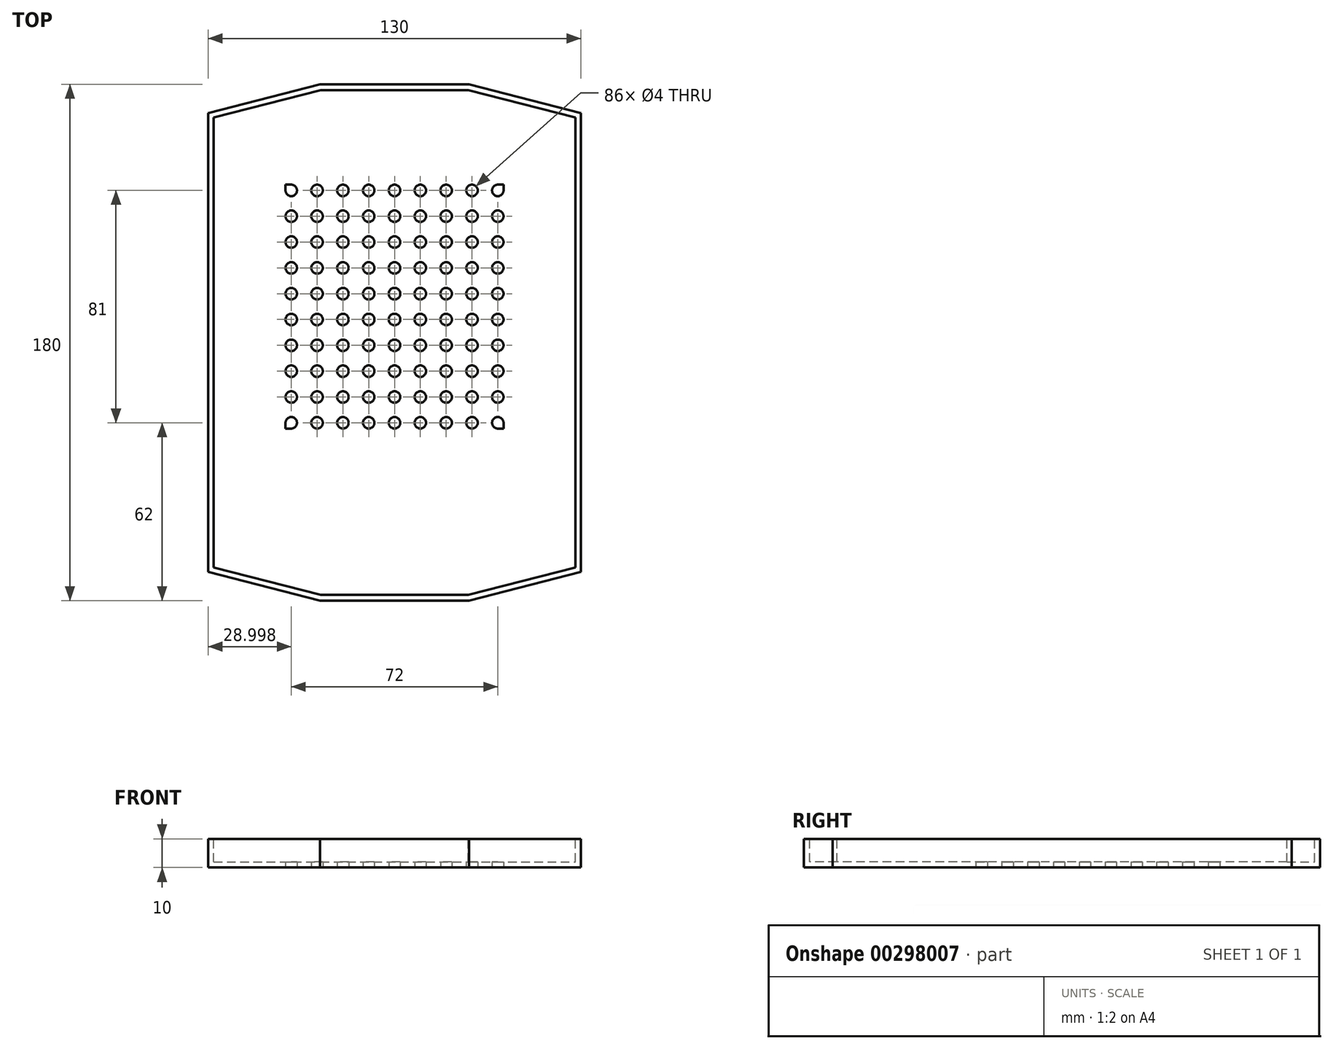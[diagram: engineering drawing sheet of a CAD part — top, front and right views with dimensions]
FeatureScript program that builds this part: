
annotation { "Feature Type Name" : "Feature", "Feature Type Description" : "" }
export const myFeature = defineFeature(function(context is Context, id is Id, definition is map)
    precondition{}
    {
        {
            var Q0;
            Q0=qCreatedBy(makeId("Top.planeOp"),FACE);
            var sketch = newSketch(context, id + "F0", { "sketchPlane" : qUnion([Q0])});
            skLineSegment(sketch, "E0.bottom", {"start": v(-77.32, -10) * mm, "end": v(52.68, -10) * mm});
            skLineSegment(sketch, "E0.top", {"start": v(-77.32, 170) * mm, "end": v(52.68, 170) * mm});
            skLineSegment(sketch, "E0.left", {"start": v(-77.32, -10) * mm, "end": v(-77.32, 170) * mm});
            skLineSegment(sketch, "E0.right", {"start": v(52.68, -10) * mm, "end": v(52.68, 170) * mm});
            skPoint(sketch, "E1", {"position": v(-38.32, 170) * mm});
            skPoint(sketch, "E2", {"position": v(-77.32, 160) * mm});
            skPoint(sketch, "E3", {"position": v(52.68, 160) * mm});
            skPoint(sketch, "E4", {"position": v(13.68, 170) * mm});
            skLineSegment(sketch, "E5", {"start": v(-77.32, 160) * mm, "end": v(-38.32, 170) * mm});
            skLineSegment(sketch, "E6", {"start": v(13.68, 170) * mm, "end": v(52.68, 160) * mm});
            skPoint(sketch, "E7", {"position": v(-77.32, 0) * mm});
            skPoint(sketch, "E8", {"position": v(-38.32, -10) * mm});
            skPoint(sketch, "E9", {"position": v(13.68, -10) * mm});
            skPoint(sketch, "E10", {"position": v(52.68, 0) * mm});
            skLineSegment(sketch, "E11", {"start": v(-77.32, 0) * mm, "end": v(-38.32, -10) * mm});
            skLineSegment(sketch, "E12", {"start": v(13.68, -10) * mm, "end": v(52.68, 0) * mm});
            skLineSegment(sketch, "E13.bottom", {"start": v(-50.32, 135) * mm, "end": v(25.68, 135) * mm});
            skLineSegment(sketch, "E13.top", {"start": v(-50.32, 50) * mm, "end": v(25.68, 50) * mm});
            skLineSegment(sketch, "E13.left", {"start": v(-50.32, 135) * mm, "end": v(-50.32, 50) * mm});
            skLineSegment(sketch, "E13.right", {"start": v(25.68, 135) * mm, "end": v(25.68, 50) * mm});
            skCircle(sketch, "E14", {"center": v(-48.32, 133) * mm, "radius": 2 * mm});
            skCircle(sketch, "E15", {"center": v(-39.32, 133) * mm, "radius": 2 * mm});
            skCircle(sketch, "E16", {"center": v(-30.32, 133) * mm, "radius": 2 * mm});
            skCircle(sketch, "E17", {"center": v(-21.32, 133) * mm, "radius": 2 * mm});
            skCircle(sketch, "E18", {"center": v(-12.32, 133) * mm, "radius": 2 * mm});
            skCircle(sketch, "E19", {"center": v(-3.32, 133) * mm, "radius": 2 * mm});
            skCircle(sketch, "E20", {"center": v(5.68, 133) * mm, "radius": 2 * mm});
            skCircle(sketch, "E21", {"center": v(14.68, 133) * mm, "radius": 2 * mm});
            skCircle(sketch, "E22", {"center": v(23.68, 133) * mm, "radius": 2 * mm});
            skCircle(sketch, "E23", {"center": v(-48.32, 124) * mm, "radius": 2 * mm});
            skCircle(sketch, "E24", {"center": v(-39.32, 124) * mm, "radius": 2 * mm});
            skCircle(sketch, "E25", {"center": v(-30.32, 124) * mm, "radius": 2 * mm});
            skCircle(sketch, "E26", {"center": v(-21.32, 124) * mm, "radius": 2 * mm});
            skCircle(sketch, "E27", {"center": v(-12.32, 124) * mm, "radius": 2 * mm});
            skCircle(sketch, "E28", {"center": v(-3.32, 124) * mm, "radius": 2 * mm});
            skCircle(sketch, "E29", {"center": v(5.68, 124) * mm, "radius": 2 * mm});
            skCircle(sketch, "E30", {"center": v(14.68, 124) * mm, "radius": 2 * mm});
            skCircle(sketch, "E31", {"center": v(23.68, 124) * mm, "radius": 2 * mm});
            skCircle(sketch, "E32", {"center": v(-48.32, 115) * mm, "radius": 2 * mm});
            skCircle(sketch, "E33", {"center": v(-39.32, 115) * mm, "radius": 2 * mm});
            skCircle(sketch, "E34", {"center": v(-30.32, 115) * mm, "radius": 2 * mm});
            skCircle(sketch, "E35", {"center": v(-21.32, 115) * mm, "radius": 2 * mm});
            skCircle(sketch, "E36", {"center": v(-12.32, 115) * mm, "radius": 2 * mm});
            skCircle(sketch, "E37", {"center": v(-3.32, 115) * mm, "radius": 2 * mm});
            skCircle(sketch, "E38", {"center": v(5.68, 115) * mm, "radius": 2 * mm});
            skCircle(sketch, "E39", {"center": v(14.68, 115) * mm, "radius": 2 * mm});
            skCircle(sketch, "E40", {"center": v(23.68, 115) * mm, "radius": 2 * mm});
            skCircle(sketch, "E41", {"center": v(-48.32, 106) * mm, "radius": 2 * mm});
            skCircle(sketch, "E42", {"center": v(-39.32, 106) * mm, "radius": 2 * mm});
            skCircle(sketch, "E43", {"center": v(-30.32, 106) * mm, "radius": 2 * mm});
            skCircle(sketch, "E44", {"center": v(-21.32, 106) * mm, "radius": 2 * mm});
            skCircle(sketch, "E45", {"center": v(-12.32, 106) * mm, "radius": 2 * mm});
            skCircle(sketch, "E46", {"center": v(-3.32, 106) * mm, "radius": 2 * mm});
            skCircle(sketch, "E47", {"center": v(5.68, 106) * mm, "radius": 2 * mm});
            skCircle(sketch, "E48", {"center": v(14.68, 106) * mm, "radius": 2 * mm});
            skCircle(sketch, "E49", {"center": v(23.68, 106) * mm, "radius": 2 * mm});
            skCircle(sketch, "E50", {"center": v(-48.32, 97) * mm, "radius": 2 * mm});
            skCircle(sketch, "E51", {"center": v(-39.32, 97) * mm, "radius": 2 * mm});
            skCircle(sketch, "E52", {"center": v(-30.32, 97) * mm, "radius": 2 * mm});
            skCircle(sketch, "E53", {"center": v(-21.32, 97) * mm, "radius": 2 * mm});
            skCircle(sketch, "E54", {"center": v(-12.32, 97) * mm, "radius": 2 * mm});
            skCircle(sketch, "E55", {"center": v(-3.32, 97) * mm, "radius": 2 * mm});
            skCircle(sketch, "E56", {"center": v(5.68, 97) * mm, "radius": 2 * mm});
            skCircle(sketch, "E57", {"center": v(14.68, 97) * mm, "radius": 2 * mm});
            skCircle(sketch, "E58", {"center": v(23.68, 97) * mm, "radius": 2 * mm});
            skCircle(sketch, "E59", {"center": v(-48.32, 88) * mm, "radius": 2 * mm});
            skCircle(sketch, "E60", {"center": v(-39.32, 88) * mm, "radius": 2 * mm});
            skCircle(sketch, "E61", {"center": v(-30.32, 88) * mm, "radius": 2 * mm});
            skCircle(sketch, "E62", {"center": v(-21.32, 88) * mm, "radius": 2 * mm});
            skCircle(sketch, "E63", {"center": v(-12.32, 88) * mm, "radius": 2 * mm});
            skCircle(sketch, "E64", {"center": v(-3.32, 88) * mm, "radius": 2 * mm});
            skCircle(sketch, "E65", {"center": v(5.68, 88) * mm, "radius": 2 * mm});
            skCircle(sketch, "E66", {"center": v(14.68, 88) * mm, "radius": 2 * mm});
            skCircle(sketch, "E67", {"center": v(23.68, 88) * mm, "radius": 2 * mm});
            skCircle(sketch, "E68", {"center": v(-48.32, 79) * mm, "radius": 2 * mm});
            skCircle(sketch, "E69", {"center": v(-39.32, 79) * mm, "radius": 2 * mm});
            skCircle(sketch, "E70", {"center": v(-30.32, 79) * mm, "radius": 2 * mm});
            skCircle(sketch, "E71", {"center": v(-21.32, 79) * mm, "radius": 2 * mm});
            skCircle(sketch, "E72", {"center": v(-12.32, 79) * mm, "radius": 2 * mm});
            skCircle(sketch, "E73", {"center": v(-3.32, 79) * mm, "radius": 2 * mm});
            skCircle(sketch, "E74", {"center": v(5.68, 79) * mm, "radius": 2 * mm});
            skCircle(sketch, "E75", {"center": v(14.68, 79) * mm, "radius": 2 * mm});
            skCircle(sketch, "E76", {"center": v(23.68, 79) * mm, "radius": 2 * mm});
            skCircle(sketch, "E77", {"center": v(-48.32, 70) * mm, "radius": 2 * mm});
            skCircle(sketch, "E78", {"center": v(-39.32, 70) * mm, "radius": 2 * mm});
            skCircle(sketch, "E79", {"center": v(-30.32, 70) * mm, "radius": 2 * mm});
            skCircle(sketch, "E80", {"center": v(-21.32, 70) * mm, "radius": 2 * mm});
            skCircle(sketch, "E81", {"center": v(-12.32, 70) * mm, "radius": 2 * mm});
            skCircle(sketch, "E82", {"center": v(-3.32, 70) * mm, "radius": 2 * mm});
            skCircle(sketch, "E83", {"center": v(5.68, 70) * mm, "radius": 2 * mm});
            skCircle(sketch, "E84", {"center": v(14.68, 70) * mm, "radius": 2 * mm});
            skCircle(sketch, "E85", {"center": v(23.68, 70) * mm, "radius": 2 * mm});
            skCircle(sketch, "E86", {"center": v(-48.32, 61) * mm, "radius": 2 * mm});
            skCircle(sketch, "E87", {"center": v(-39.32, 61) * mm, "radius": 2 * mm});
            skCircle(sketch, "E88", {"center": v(-30.32, 61) * mm, "radius": 2 * mm});
            skCircle(sketch, "E89", {"center": v(-21.32, 61) * mm, "radius": 2 * mm});
            skCircle(sketch, "E90", {"center": v(-12.32, 61) * mm, "radius": 2 * mm});
            skCircle(sketch, "E91", {"center": v(-3.32, 61) * mm, "radius": 2 * mm});
            skCircle(sketch, "E92", {"center": v(5.68, 61) * mm, "radius": 2 * mm});
            skCircle(sketch, "E93", {"center": v(14.68, 61) * mm, "radius": 2 * mm});
            skCircle(sketch, "E94", {"center": v(23.68, 61) * mm, "radius": 2 * mm});
            skCircle(sketch, "E95", {"center": v(-48.32, 52) * mm, "radius": 2 * mm});
            skCircle(sketch, "E96", {"center": v(-39.32, 52) * mm, "radius": 2 * mm});
            skCircle(sketch, "E97", {"center": v(-30.32, 52) * mm, "radius": 2 * mm});
            skCircle(sketch, "E98", {"center": v(-21.32, 52) * mm, "radius": 2 * mm});
            skCircle(sketch, "E99", {"center": v(-12.32, 52) * mm, "radius": 2 * mm});
            skCircle(sketch, "E100", {"center": v(-3.32, 52) * mm, "radius": 2 * mm});
            skCircle(sketch, "E101", {"center": v(5.68, 52) * mm, "radius": 2 * mm});
            skCircle(sketch, "E102", {"center": v(14.68, 52) * mm, "radius": 2 * mm});
            skCircle(sketch, "E103", {"center": v(23.68, 52) * mm, "radius": 2 * mm});
            skSolve(sketch);
        }
        {
            var Q0;
            {var subQ39=sQuery(id+"F0.wireOp",EDGE,"E5");Q0=makeQuery(id+"F0.imprint","IMPRINT",FACE,{"disambiguationData":[TD([[makeQuery(id+"F0.imprint","IMPRINT",EDGE,{"derivedFrom":subQ39}),-1.0]])]});}
            var Q1;
            {var subQ43=sQuery(id+"F0.wireOp",EDGE,"E15");Q1=makeQuery(id+"F0.imprint","IMPRINT",FACE,{"disambiguationData":[TD([[makeQuery(id+"F0.imprint","IMPRINT",EDGE,{"derivedFrom":subQ43}),-1.0]])]});}
            extrude(context, id + "F1", {"entities" : qUnion([Q0, Q1]), "depth" : 10 * mm});
        }
        {
            var Q0;
            Q0=makeQuery(id+"F1.opExtrude","CAP_FACE",FACE,{"disambiguationData":[OSD([sQuery(id+"F0.wireOp",EDGE,"E0.bottom"),sQuery(id+"F0.wireOp",EDGE,"E0.top"),sQuery(id+"F0.wireOp",EDGE,"E0.left"),sQuery(id+"F0.wireOp",EDGE,"E0.right"),sQuery(id+"F0.wireOp",EDGE,"E5"),sQuery(id+"F0.wireOp",EDGE,"E6"),sQuery(id+"F0.wireOp",EDGE,"E11"),sQuery(id+"F0.wireOp",EDGE,"E12"),sQuery(id+"F0.wireOp",EDGE,"E13.bottom"),sQuery(id+"F0.wireOp",EDGE,"E13.top"),sQuery(id+"F0.wireOp",EDGE,"E13.left"),sQuery(id+"F0.wireOp",EDGE,"E13.right"),sQuery(id+"F0.wireOp",EDGE,"E14"),sQuery(id+"F0.wireOp",EDGE,"E15"),sQuery(id+"F0.wireOp",EDGE,"E16"),sQuery(id+"F0.wireOp",EDGE,"E17"),sQuery(id+"F0.wireOp",EDGE,"E18"),sQuery(id+"F0.wireOp",EDGE,"E19"),sQuery(id+"F0.wireOp",EDGE,"E20"),sQuery(id+"F0.wireOp",EDGE,"E21"),sQuery(id+"F0.wireOp",EDGE,"E22"),sQuery(id+"F0.wireOp",EDGE,"E23"),sQuery(id+"F0.wireOp",EDGE,"E24"),sQuery(id+"F0.wireOp",EDGE,"E25"),sQuery(id+"F0.wireOp",EDGE,"E26"),sQuery(id+"F0.wireOp",EDGE,"E27"),sQuery(id+"F0.wireOp",EDGE,"E28"),sQuery(id+"F0.wireOp",EDGE,"E29"),sQuery(id+"F0.wireOp",EDGE,"E30"),sQuery(id+"F0.wireOp",EDGE,"E31"),sQuery(id+"F0.wireOp",EDGE,"E32"),sQuery(id+"F0.wireOp",EDGE,"E33"),sQuery(id+"F0.wireOp",EDGE,"E34"),sQuery(id+"F0.wireOp",EDGE,"E35"),sQuery(id+"F0.wireOp",EDGE,"E36"),sQuery(id+"F0.wireOp",EDGE,"E37"),sQuery(id+"F0.wireOp",EDGE,"E38"),sQuery(id+"F0.wireOp",EDGE,"E39"),sQuery(id+"F0.wireOp",EDGE,"E40"),sQuery(id+"F0.wireOp",EDGE,"E41"),sQuery(id+"F0.wireOp",EDGE,"E42"),sQuery(id+"F0.wireOp",EDGE,"E43"),sQuery(id+"F0.wireOp",EDGE,"E44"),sQuery(id+"F0.wireOp",EDGE,"E45"),sQuery(id+"F0.wireOp",EDGE,"E46"),sQuery(id+"F0.wireOp",EDGE,"E47"),sQuery(id+"F0.wireOp",EDGE,"E48"),sQuery(id+"F0.wireOp",EDGE,"E49"),sQuery(id+"F0.wireOp",EDGE,"E50"),sQuery(id+"F0.wireOp",EDGE,"E51"),sQuery(id+"F0.wireOp",EDGE,"E52"),sQuery(id+"F0.wireOp",EDGE,"E53"),sQuery(id+"F0.wireOp",EDGE,"E54"),sQuery(id+"F0.wireOp",EDGE,"E55"),sQuery(id+"F0.wireOp",EDGE,"E56"),sQuery(id+"F0.wireOp",EDGE,"E57"),sQuery(id+"F0.wireOp",EDGE,"E58"),sQuery(id+"F0.wireOp",EDGE,"E59"),sQuery(id+"F0.wireOp",EDGE,"E60"),sQuery(id+"F0.wireOp",EDGE,"E61"),sQuery(id+"F0.wireOp",EDGE,"E62"),sQuery(id+"F0.wireOp",EDGE,"E63"),sQuery(id+"F0.wireOp",EDGE,"E64"),sQuery(id+"F0.wireOp",EDGE,"E65"),sQuery(id+"F0.wireOp",EDGE,"E66"),sQuery(id+"F0.wireOp",EDGE,"E67"),sQuery(id+"F0.wireOp",EDGE,"E68"),sQuery(id+"F0.wireOp",EDGE,"E69"),sQuery(id+"F0.wireOp",EDGE,"E70"),sQuery(id+"F0.wireOp",EDGE,"E71"),sQuery(id+"F0.wireOp",EDGE,"E72"),sQuery(id+"F0.wireOp",EDGE,"E73"),sQuery(id+"F0.wireOp",EDGE,"E74"),sQuery(id+"F0.wireOp",EDGE,"E75"),sQuery(id+"F0.wireOp",EDGE,"E76"),sQuery(id+"F0.wireOp",EDGE,"E77"),sQuery(id+"F0.wireOp",EDGE,"E78"),sQuery(id+"F0.wireOp",EDGE,"E79"),sQuery(id+"F0.wireOp",EDGE,"E80"),sQuery(id+"F0.wireOp",EDGE,"E81"),sQuery(id+"F0.wireOp",EDGE,"E82"),sQuery(id+"F0.wireOp",EDGE,"E83"),sQuery(id+"F0.wireOp",EDGE,"E84"),sQuery(id+"F0.wireOp",EDGE,"E85"),sQuery(id+"F0.wireOp",EDGE,"E86"),sQuery(id+"F0.wireOp",EDGE,"E87"),sQuery(id+"F0.wireOp",EDGE,"E88"),sQuery(id+"F0.wireOp",EDGE,"E89"),sQuery(id+"F0.wireOp",EDGE,"E90"),sQuery(id+"F0.wireOp",EDGE,"E91"),sQuery(id+"F0.wireOp",EDGE,"E92"),sQuery(id+"F0.wireOp",EDGE,"E93"),sQuery(id+"F0.wireOp",EDGE,"E94"),sQuery(id+"F0.wireOp",EDGE,"E95"),sQuery(id+"F0.wireOp",EDGE,"E96"),sQuery(id+"F0.wireOp",EDGE,"E97"),sQuery(id+"F0.wireOp",EDGE,"E98"),sQuery(id+"F0.wireOp",EDGE,"E99"),sQuery(id+"F0.wireOp",EDGE,"E100"),sQuery(id+"F0.wireOp",EDGE,"E101"),sQuery(id+"F0.wireOp",EDGE,"E102"),sQuery(id+"F0.wireOp",EDGE,"E103")])],"isStart":false});
            var sketch = newSketch(context, id + "F2", { "sketchPlane" : qUnion([Q0])});
            skLineSegment(sketch, "E104.bottom", {"start": v(-75.32, 168) * mm, "end": v(50.68, 168) * mm});
            skLineSegment(sketch, "E104.top", {"start": v(-75.32, -8) * mm, "end": v(50.68, -8) * mm});
            skLineSegment(sketch, "E104.left", {"start": v(-75.32, 168) * mm, "end": v(-75.32, -8) * mm});
            skLineSegment(sketch, "E104.right", {"start": v(50.68, 168) * mm, "end": v(50.68, -8) * mm});
            skLineSegment(sketch, "E105", {"start": v(-75.32, 158.45) * mm, "end": v(-38.07, 168) * mm});
            skLineSegment(sketch, "E106", {"start": v(13.43, 168) * mm, "end": v(50.68, 158.45) * mm});
            skLineSegment(sketch, "E107", {"start": v(-75.32, 1.55) * mm, "end": v(-38.07, -8) * mm});
            skLineSegment(sketch, "E108", {"start": v(13.43, -8) * mm, "end": v(50.68, 1.55) * mm});
            skSolve(sketch);
        }
        {
            var Q0;
            {var subQ3=sQuery(id+"F0.wireOp",EDGE,"E14");Q0=makeQuery(id+"F2.imprint","IMPRINT",FACE,{"disambiguationData":[TD([[makeQuery(id+"F2.imprint","IMPRINT",EDGE,{"derivedFrom":makeQuery(id+"F1.opExtrude","CAP_EDGE",EDGE,{"disambiguationData":[OSD([subQ3])],"isStart":false})}),1.0]])]});}
            var Q1;
            {var subQ3=sQuery(id+"F0.wireOp",EDGE,"E22");Q1=makeQuery(id+"F2.imprint","IMPRINT",FACE,{"disambiguationData":[TD([[makeQuery(id+"F2.imprint","IMPRINT",EDGE,{"derivedFrom":makeQuery(id+"F1.opExtrude","CAP_EDGE",EDGE,{"disambiguationData":[OSD([subQ3])],"isStart":false})}),1.0]])]});}
            var Q2;
            {var subQ3=sQuery(id+"F0.wireOp",EDGE,"E95");Q2=makeQuery(id+"F2.imprint","IMPRINT",FACE,{"disambiguationData":[TD([[makeQuery(id+"F2.imprint","IMPRINT",EDGE,{"derivedFrom":makeQuery(id+"F1.opExtrude","CAP_EDGE",EDGE,{"disambiguationData":[OSD([subQ3])],"isStart":false})}),1.0]])]});}
            var Q3;
            {var subQ3=sQuery(id+"F0.wireOp",EDGE,"E103");Q3=makeQuery(id+"F2.imprint","IMPRINT",FACE,{"disambiguationData":[TD([[makeQuery(id+"F2.imprint","IMPRINT",EDGE,{"derivedFrom":makeQuery(id+"F1.opExtrude","CAP_EDGE",EDGE,{"disambiguationData":[OSD([subQ3])],"isStart":false})}),1.0]])]});}
            var Q4;
            Q4=makeQuery(id+"F2.imprint","IMPRINT",FACE,{"disambiguationData":[TD([[makeQuery(id+"F2.imprint","IMPRINT",EDGE,{"derivedFrom":makeQuery(id+"F1.opExtrude","CAP_EDGE",EDGE,{"disambiguationData":[OSD([sQuery(id+"F0.wireOp",EDGE,"E15")])],"isStart":false})}),1.0]])]});
            var Q5;
            Q5=makeQuery(id+"F2.imprint","IMPRINT",FACE,{"disambiguationData":[TD([[makeQuery(id+"F2.imprint","IMPRINT",EDGE,{"derivedFrom":makeQuery(id+"F1.opExtrude","CAP_EDGE",EDGE,{"disambiguationData":[OSD([sQuery(id+"F0.wireOp",EDGE,"E16")])],"isStart":false})}),1.0]])]});
            var Q6;
            Q6=makeQuery(id+"F2.imprint","IMPRINT",FACE,{"disambiguationData":[TD([[makeQuery(id+"F2.imprint","IMPRINT",EDGE,{"derivedFrom":makeQuery(id+"F1.opExtrude","CAP_EDGE",EDGE,{"disambiguationData":[OSD([sQuery(id+"F0.wireOp",EDGE,"E17")])],"isStart":false})}),1.0]])]});
            var Q7;
            Q7=makeQuery(id+"F2.imprint","IMPRINT",FACE,{"disambiguationData":[TD([[makeQuery(id+"F2.imprint","IMPRINT",EDGE,{"derivedFrom":makeQuery(id+"F1.opExtrude","CAP_EDGE",EDGE,{"disambiguationData":[OSD([sQuery(id+"F0.wireOp",EDGE,"E18")])],"isStart":false})}),1.0]])]});
            var Q8;
            Q8=makeQuery(id+"F2.imprint","IMPRINT",FACE,{"disambiguationData":[TD([[makeQuery(id+"F2.imprint","IMPRINT",EDGE,{"derivedFrom":makeQuery(id+"F1.opExtrude","CAP_EDGE",EDGE,{"disambiguationData":[OSD([sQuery(id+"F0.wireOp",EDGE,"E19")])],"isStart":false})}),1.0]])]});
            var Q9;
            Q9=makeQuery(id+"F2.imprint","IMPRINT",FACE,{"disambiguationData":[TD([[makeQuery(id+"F2.imprint","IMPRINT",EDGE,{"derivedFrom":makeQuery(id+"F1.opExtrude","CAP_EDGE",EDGE,{"disambiguationData":[OSD([sQuery(id+"F0.wireOp",EDGE,"E20")])],"isStart":false})}),1.0]])]});
            var Q10;
            Q10=makeQuery(id+"F2.imprint","IMPRINT",FACE,{"disambiguationData":[TD([[makeQuery(id+"F2.imprint","IMPRINT",EDGE,{"derivedFrom":makeQuery(id+"F1.opExtrude","CAP_EDGE",EDGE,{"disambiguationData":[OSD([sQuery(id+"F0.wireOp",EDGE,"E21")])],"isStart":false})}),1.0]])]});
            var Q11;
            Q11=makeQuery(id+"F2.imprint","IMPRINT",FACE,{"disambiguationData":[TD([[makeQuery(id+"F2.imprint","IMPRINT",EDGE,{"derivedFrom":makeQuery(id+"F1.opExtrude","CAP_EDGE",EDGE,{"disambiguationData":[OSD([sQuery(id+"F0.wireOp",EDGE,"E23")])],"isStart":false})}),1.0]])]});
            var Q12;
            Q12=makeQuery(id+"F2.imprint","IMPRINT",FACE,{"disambiguationData":[TD([[makeQuery(id+"F2.imprint","IMPRINT",EDGE,{"derivedFrom":makeQuery(id+"F1.opExtrude","CAP_EDGE",EDGE,{"disambiguationData":[OSD([sQuery(id+"F0.wireOp",EDGE,"E24")])],"isStart":false})}),1.0]])]});
            var Q13;
            Q13=makeQuery(id+"F2.imprint","IMPRINT",FACE,{"disambiguationData":[TD([[makeQuery(id+"F2.imprint","IMPRINT",EDGE,{"derivedFrom":makeQuery(id+"F1.opExtrude","CAP_EDGE",EDGE,{"disambiguationData":[OSD([sQuery(id+"F0.wireOp",EDGE,"E25")])],"isStart":false})}),1.0]])]});
            var Q14;
            Q14=makeQuery(id+"F2.imprint","IMPRINT",FACE,{"disambiguationData":[TD([[makeQuery(id+"F2.imprint","IMPRINT",EDGE,{"derivedFrom":makeQuery(id+"F1.opExtrude","CAP_EDGE",EDGE,{"disambiguationData":[OSD([sQuery(id+"F0.wireOp",EDGE,"E26")])],"isStart":false})}),1.0]])]});
            var Q15;
            Q15=makeQuery(id+"F2.imprint","IMPRINT",FACE,{"disambiguationData":[TD([[makeQuery(id+"F2.imprint","IMPRINT",EDGE,{"derivedFrom":makeQuery(id+"F1.opExtrude","CAP_EDGE",EDGE,{"disambiguationData":[OSD([sQuery(id+"F0.wireOp",EDGE,"E27")])],"isStart":false})}),1.0]])]});
            var Q16;
            Q16=makeQuery(id+"F2.imprint","IMPRINT",FACE,{"disambiguationData":[TD([[makeQuery(id+"F2.imprint","IMPRINT",EDGE,{"derivedFrom":makeQuery(id+"F1.opExtrude","CAP_EDGE",EDGE,{"disambiguationData":[OSD([sQuery(id+"F0.wireOp",EDGE,"E28")])],"isStart":false})}),1.0]])]});
            var Q17;
            Q17=makeQuery(id+"F2.imprint","IMPRINT",FACE,{"disambiguationData":[TD([[makeQuery(id+"F2.imprint","IMPRINT",EDGE,{"derivedFrom":makeQuery(id+"F1.opExtrude","CAP_EDGE",EDGE,{"disambiguationData":[OSD([sQuery(id+"F0.wireOp",EDGE,"E29")])],"isStart":false})}),1.0]])]});
            var Q18;
            Q18=makeQuery(id+"F2.imprint","IMPRINT",FACE,{"disambiguationData":[TD([[makeQuery(id+"F2.imprint","IMPRINT",EDGE,{"derivedFrom":makeQuery(id+"F1.opExtrude","CAP_EDGE",EDGE,{"disambiguationData":[OSD([sQuery(id+"F0.wireOp",EDGE,"E30")])],"isStart":false})}),1.0]])]});
            var Q19;
            Q19=makeQuery(id+"F2.imprint","IMPRINT",FACE,{"disambiguationData":[TD([[makeQuery(id+"F2.imprint","IMPRINT",EDGE,{"derivedFrom":makeQuery(id+"F1.opExtrude","CAP_EDGE",EDGE,{"disambiguationData":[OSD([sQuery(id+"F0.wireOp",EDGE,"E31")])],"isStart":false})}),1.0]])]});
            var Q20;
            Q20=makeQuery(id+"F2.imprint","IMPRINT",FACE,{"disambiguationData":[TD([[makeQuery(id+"F2.imprint","IMPRINT",EDGE,{"derivedFrom":makeQuery(id+"F1.opExtrude","CAP_EDGE",EDGE,{"disambiguationData":[OSD([sQuery(id+"F0.wireOp",EDGE,"E32")])],"isStart":false})}),1.0]])]});
            var Q21;
            Q21=makeQuery(id+"F2.imprint","IMPRINT",FACE,{"disambiguationData":[TD([[makeQuery(id+"F2.imprint","IMPRINT",EDGE,{"derivedFrom":makeQuery(id+"F1.opExtrude","CAP_EDGE",EDGE,{"disambiguationData":[OSD([sQuery(id+"F0.wireOp",EDGE,"E33")])],"isStart":false})}),1.0]])]});
            var Q22;
            Q22=makeQuery(id+"F2.imprint","IMPRINT",FACE,{"disambiguationData":[TD([[makeQuery(id+"F2.imprint","IMPRINT",EDGE,{"derivedFrom":makeQuery(id+"F1.opExtrude","CAP_EDGE",EDGE,{"disambiguationData":[OSD([sQuery(id+"F0.wireOp",EDGE,"E34")])],"isStart":false})}),1.0]])]});
            var Q23;
            Q23=makeQuery(id+"F2.imprint","IMPRINT",FACE,{"disambiguationData":[TD([[makeQuery(id+"F2.imprint","IMPRINT",EDGE,{"derivedFrom":makeQuery(id+"F1.opExtrude","CAP_EDGE",EDGE,{"disambiguationData":[OSD([sQuery(id+"F0.wireOp",EDGE,"E35")])],"isStart":false})}),1.0]])]});
            var Q24;
            Q24=makeQuery(id+"F2.imprint","IMPRINT",FACE,{"disambiguationData":[TD([[makeQuery(id+"F2.imprint","IMPRINT",EDGE,{"derivedFrom":makeQuery(id+"F1.opExtrude","CAP_EDGE",EDGE,{"disambiguationData":[OSD([sQuery(id+"F0.wireOp",EDGE,"E36")])],"isStart":false})}),1.0]])]});
            var Q25;
            Q25=makeQuery(id+"F2.imprint","IMPRINT",FACE,{"disambiguationData":[TD([[makeQuery(id+"F2.imprint","IMPRINT",EDGE,{"derivedFrom":makeQuery(id+"F1.opExtrude","CAP_EDGE",EDGE,{"disambiguationData":[OSD([sQuery(id+"F0.wireOp",EDGE,"E37")])],"isStart":false})}),1.0]])]});
            var Q26;
            Q26=makeQuery(id+"F2.imprint","IMPRINT",FACE,{"disambiguationData":[TD([[makeQuery(id+"F2.imprint","IMPRINT",EDGE,{"derivedFrom":makeQuery(id+"F1.opExtrude","CAP_EDGE",EDGE,{"disambiguationData":[OSD([sQuery(id+"F0.wireOp",EDGE,"E38")])],"isStart":false})}),1.0]])]});
            var Q27;
            Q27=makeQuery(id+"F2.imprint","IMPRINT",FACE,{"disambiguationData":[TD([[makeQuery(id+"F2.imprint","IMPRINT",EDGE,{"derivedFrom":makeQuery(id+"F1.opExtrude","CAP_EDGE",EDGE,{"disambiguationData":[OSD([sQuery(id+"F0.wireOp",EDGE,"E39")])],"isStart":false})}),1.0]])]});
            var Q28;
            Q28=makeQuery(id+"F2.imprint","IMPRINT",FACE,{"disambiguationData":[TD([[makeQuery(id+"F2.imprint","IMPRINT",EDGE,{"derivedFrom":makeQuery(id+"F1.opExtrude","CAP_EDGE",EDGE,{"disambiguationData":[OSD([sQuery(id+"F0.wireOp",EDGE,"E40")])],"isStart":false})}),1.0]])]});
            var Q29;
            Q29=makeQuery(id+"F2.imprint","IMPRINT",FACE,{"disambiguationData":[TD([[makeQuery(id+"F2.imprint","IMPRINT",EDGE,{"derivedFrom":makeQuery(id+"F1.opExtrude","CAP_EDGE",EDGE,{"disambiguationData":[OSD([sQuery(id+"F0.wireOp",EDGE,"E41")])],"isStart":false})}),1.0]])]});
            var Q30;
            Q30=makeQuery(id+"F2.imprint","IMPRINT",FACE,{"disambiguationData":[TD([[makeQuery(id+"F2.imprint","IMPRINT",EDGE,{"derivedFrom":makeQuery(id+"F1.opExtrude","CAP_EDGE",EDGE,{"disambiguationData":[OSD([sQuery(id+"F0.wireOp",EDGE,"E42")])],"isStart":false})}),1.0]])]});
            var Q31;
            Q31=makeQuery(id+"F2.imprint","IMPRINT",FACE,{"disambiguationData":[TD([[makeQuery(id+"F2.imprint","IMPRINT",EDGE,{"derivedFrom":makeQuery(id+"F1.opExtrude","CAP_EDGE",EDGE,{"disambiguationData":[OSD([sQuery(id+"F0.wireOp",EDGE,"E43")])],"isStart":false})}),1.0]])]});
            var Q32;
            Q32=makeQuery(id+"F2.imprint","IMPRINT",FACE,{"disambiguationData":[TD([[makeQuery(id+"F2.imprint","IMPRINT",EDGE,{"derivedFrom":makeQuery(id+"F1.opExtrude","CAP_EDGE",EDGE,{"disambiguationData":[OSD([sQuery(id+"F0.wireOp",EDGE,"E44")])],"isStart":false})}),1.0]])]});
            var Q33;
            Q33=makeQuery(id+"F2.imprint","IMPRINT",FACE,{"disambiguationData":[TD([[makeQuery(id+"F2.imprint","IMPRINT",EDGE,{"derivedFrom":makeQuery(id+"F1.opExtrude","CAP_EDGE",EDGE,{"disambiguationData":[OSD([sQuery(id+"F0.wireOp",EDGE,"E45")])],"isStart":false})}),1.0]])]});
            var Q34;
            Q34=makeQuery(id+"F2.imprint","IMPRINT",FACE,{"disambiguationData":[TD([[makeQuery(id+"F2.imprint","IMPRINT",EDGE,{"derivedFrom":makeQuery(id+"F1.opExtrude","CAP_EDGE",EDGE,{"disambiguationData":[OSD([sQuery(id+"F0.wireOp",EDGE,"E46")])],"isStart":false})}),1.0]])]});
            var Q35;
            Q35=makeQuery(id+"F2.imprint","IMPRINT",FACE,{"disambiguationData":[TD([[makeQuery(id+"F2.imprint","IMPRINT",EDGE,{"derivedFrom":makeQuery(id+"F1.opExtrude","CAP_EDGE",EDGE,{"disambiguationData":[OSD([sQuery(id+"F0.wireOp",EDGE,"E47")])],"isStart":false})}),1.0]])]});
            var Q36;
            Q36=makeQuery(id+"F2.imprint","IMPRINT",FACE,{"disambiguationData":[TD([[makeQuery(id+"F2.imprint","IMPRINT",EDGE,{"derivedFrom":makeQuery(id+"F1.opExtrude","CAP_EDGE",EDGE,{"disambiguationData":[OSD([sQuery(id+"F0.wireOp",EDGE,"E48")])],"isStart":false})}),1.0]])]});
            var Q37;
            Q37=makeQuery(id+"F2.imprint","IMPRINT",FACE,{"disambiguationData":[TD([[makeQuery(id+"F2.imprint","IMPRINT",EDGE,{"derivedFrom":makeQuery(id+"F1.opExtrude","CAP_EDGE",EDGE,{"disambiguationData":[OSD([sQuery(id+"F0.wireOp",EDGE,"E49")])],"isStart":false})}),1.0]])]});
            var Q38;
            Q38=makeQuery(id+"F2.imprint","IMPRINT",FACE,{"disambiguationData":[TD([[makeQuery(id+"F2.imprint","IMPRINT",EDGE,{"derivedFrom":makeQuery(id+"F1.opExtrude","CAP_EDGE",EDGE,{"disambiguationData":[OSD([sQuery(id+"F0.wireOp",EDGE,"E50")])],"isStart":false})}),1.0]])]});
            var Q39;
            Q39=makeQuery(id+"F2.imprint","IMPRINT",FACE,{"disambiguationData":[TD([[makeQuery(id+"F2.imprint","IMPRINT",EDGE,{"derivedFrom":makeQuery(id+"F1.opExtrude","CAP_EDGE",EDGE,{"disambiguationData":[OSD([sQuery(id+"F0.wireOp",EDGE,"E51")])],"isStart":false})}),1.0]])]});
            var Q40;
            Q40=makeQuery(id+"F2.imprint","IMPRINT",FACE,{"disambiguationData":[TD([[makeQuery(id+"F2.imprint","IMPRINT",EDGE,{"derivedFrom":makeQuery(id+"F1.opExtrude","CAP_EDGE",EDGE,{"disambiguationData":[OSD([sQuery(id+"F0.wireOp",EDGE,"E52")])],"isStart":false})}),1.0]])]});
            var Q41;
            Q41=makeQuery(id+"F2.imprint","IMPRINT",FACE,{"disambiguationData":[TD([[makeQuery(id+"F2.imprint","IMPRINT",EDGE,{"derivedFrom":makeQuery(id+"F1.opExtrude","CAP_EDGE",EDGE,{"disambiguationData":[OSD([sQuery(id+"F0.wireOp",EDGE,"E53")])],"isStart":false})}),1.0]])]});
            var Q42;
            Q42=makeQuery(id+"F2.imprint","IMPRINT",FACE,{"disambiguationData":[TD([[makeQuery(id+"F2.imprint","IMPRINT",EDGE,{"derivedFrom":makeQuery(id+"F1.opExtrude","CAP_EDGE",EDGE,{"disambiguationData":[OSD([sQuery(id+"F0.wireOp",EDGE,"E54")])],"isStart":false})}),1.0]])]});
            var Q43;
            Q43=makeQuery(id+"F2.imprint","IMPRINT",FACE,{"disambiguationData":[TD([[makeQuery(id+"F2.imprint","IMPRINT",EDGE,{"derivedFrom":makeQuery(id+"F1.opExtrude","CAP_EDGE",EDGE,{"disambiguationData":[OSD([sQuery(id+"F0.wireOp",EDGE,"E55")])],"isStart":false})}),1.0]])]});
            var Q44;
            Q44=makeQuery(id+"F2.imprint","IMPRINT",FACE,{"disambiguationData":[TD([[makeQuery(id+"F2.imprint","IMPRINT",EDGE,{"derivedFrom":makeQuery(id+"F1.opExtrude","CAP_EDGE",EDGE,{"disambiguationData":[OSD([sQuery(id+"F0.wireOp",EDGE,"E56")])],"isStart":false})}),1.0]])]});
            var Q45;
            Q45=makeQuery(id+"F2.imprint","IMPRINT",FACE,{"disambiguationData":[TD([[makeQuery(id+"F2.imprint","IMPRINT",EDGE,{"derivedFrom":makeQuery(id+"F1.opExtrude","CAP_EDGE",EDGE,{"disambiguationData":[OSD([sQuery(id+"F0.wireOp",EDGE,"E57")])],"isStart":false})}),1.0]])]});
            var Q46;
            Q46=makeQuery(id+"F2.imprint","IMPRINT",FACE,{"disambiguationData":[TD([[makeQuery(id+"F2.imprint","IMPRINT",EDGE,{"derivedFrom":makeQuery(id+"F1.opExtrude","CAP_EDGE",EDGE,{"disambiguationData":[OSD([sQuery(id+"F0.wireOp",EDGE,"E58")])],"isStart":false})}),1.0]])]});
            var Q47;
            Q47=makeQuery(id+"F2.imprint","IMPRINT",FACE,{"disambiguationData":[TD([[makeQuery(id+"F2.imprint","IMPRINT",EDGE,{"derivedFrom":makeQuery(id+"F1.opExtrude","CAP_EDGE",EDGE,{"disambiguationData":[OSD([sQuery(id+"F0.wireOp",EDGE,"E59")])],"isStart":false})}),1.0]])]});
            var Q48;
            Q48=makeQuery(id+"F2.imprint","IMPRINT",FACE,{"disambiguationData":[TD([[makeQuery(id+"F2.imprint","IMPRINT",EDGE,{"derivedFrom":makeQuery(id+"F1.opExtrude","CAP_EDGE",EDGE,{"disambiguationData":[OSD([sQuery(id+"F0.wireOp",EDGE,"E60")])],"isStart":false})}),1.0]])]});
            var Q49;
            Q49=makeQuery(id+"F2.imprint","IMPRINT",FACE,{"disambiguationData":[TD([[makeQuery(id+"F2.imprint","IMPRINT",EDGE,{"derivedFrom":makeQuery(id+"F1.opExtrude","CAP_EDGE",EDGE,{"disambiguationData":[OSD([sQuery(id+"F0.wireOp",EDGE,"E61")])],"isStart":false})}),1.0]])]});
            var Q50;
            Q50=makeQuery(id+"F2.imprint","IMPRINT",FACE,{"disambiguationData":[TD([[makeQuery(id+"F2.imprint","IMPRINT",EDGE,{"derivedFrom":makeQuery(id+"F1.opExtrude","CAP_EDGE",EDGE,{"disambiguationData":[OSD([sQuery(id+"F0.wireOp",EDGE,"E62")])],"isStart":false})}),1.0]])]});
            var Q51;
            Q51=makeQuery(id+"F2.imprint","IMPRINT",FACE,{"disambiguationData":[TD([[makeQuery(id+"F2.imprint","IMPRINT",EDGE,{"derivedFrom":makeQuery(id+"F1.opExtrude","CAP_EDGE",EDGE,{"disambiguationData":[OSD([sQuery(id+"F0.wireOp",EDGE,"E63")])],"isStart":false})}),1.0]])]});
            var Q52;
            Q52=makeQuery(id+"F2.imprint","IMPRINT",FACE,{"disambiguationData":[TD([[makeQuery(id+"F2.imprint","IMPRINT",EDGE,{"derivedFrom":makeQuery(id+"F1.opExtrude","CAP_EDGE",EDGE,{"disambiguationData":[OSD([sQuery(id+"F0.wireOp",EDGE,"E64")])],"isStart":false})}),1.0]])]});
            var Q53;
            Q53=makeQuery(id+"F2.imprint","IMPRINT",FACE,{"disambiguationData":[TD([[makeQuery(id+"F2.imprint","IMPRINT",EDGE,{"derivedFrom":makeQuery(id+"F1.opExtrude","CAP_EDGE",EDGE,{"disambiguationData":[OSD([sQuery(id+"F0.wireOp",EDGE,"E65")])],"isStart":false})}),1.0]])]});
            var Q54;
            Q54=makeQuery(id+"F2.imprint","IMPRINT",FACE,{"disambiguationData":[TD([[makeQuery(id+"F2.imprint","IMPRINT",EDGE,{"derivedFrom":makeQuery(id+"F1.opExtrude","CAP_EDGE",EDGE,{"disambiguationData":[OSD([sQuery(id+"F0.wireOp",EDGE,"E66")])],"isStart":false})}),1.0]])]});
            var Q55;
            Q55=makeQuery(id+"F2.imprint","IMPRINT",FACE,{"disambiguationData":[TD([[makeQuery(id+"F2.imprint","IMPRINT",EDGE,{"derivedFrom":makeQuery(id+"F1.opExtrude","CAP_EDGE",EDGE,{"disambiguationData":[OSD([sQuery(id+"F0.wireOp",EDGE,"E67")])],"isStart":false})}),1.0]])]});
            var Q56;
            Q56=makeQuery(id+"F2.imprint","IMPRINT",FACE,{"disambiguationData":[TD([[makeQuery(id+"F2.imprint","IMPRINT",EDGE,{"derivedFrom":makeQuery(id+"F1.opExtrude","CAP_EDGE",EDGE,{"disambiguationData":[OSD([sQuery(id+"F0.wireOp",EDGE,"E68")])],"isStart":false})}),1.0]])]});
            var Q57;
            Q57=makeQuery(id+"F2.imprint","IMPRINT",FACE,{"disambiguationData":[TD([[makeQuery(id+"F2.imprint","IMPRINT",EDGE,{"derivedFrom":makeQuery(id+"F1.opExtrude","CAP_EDGE",EDGE,{"disambiguationData":[OSD([sQuery(id+"F0.wireOp",EDGE,"E69")])],"isStart":false})}),1.0]])]});
            var Q58;
            Q58=makeQuery(id+"F2.imprint","IMPRINT",FACE,{"disambiguationData":[TD([[makeQuery(id+"F2.imprint","IMPRINT",EDGE,{"derivedFrom":makeQuery(id+"F1.opExtrude","CAP_EDGE",EDGE,{"disambiguationData":[OSD([sQuery(id+"F0.wireOp",EDGE,"E70")])],"isStart":false})}),1.0]])]});
            var Q59;
            Q59=makeQuery(id+"F2.imprint","IMPRINT",FACE,{"disambiguationData":[TD([[makeQuery(id+"F2.imprint","IMPRINT",EDGE,{"derivedFrom":makeQuery(id+"F1.opExtrude","CAP_EDGE",EDGE,{"disambiguationData":[OSD([sQuery(id+"F0.wireOp",EDGE,"E71")])],"isStart":false})}),1.0]])]});
            var Q60;
            Q60=makeQuery(id+"F2.imprint","IMPRINT",FACE,{"disambiguationData":[TD([[makeQuery(id+"F2.imprint","IMPRINT",EDGE,{"derivedFrom":makeQuery(id+"F1.opExtrude","CAP_EDGE",EDGE,{"disambiguationData":[OSD([sQuery(id+"F0.wireOp",EDGE,"E72")])],"isStart":false})}),1.0]])]});
            var Q61;
            Q61=makeQuery(id+"F2.imprint","IMPRINT",FACE,{"disambiguationData":[TD([[makeQuery(id+"F2.imprint","IMPRINT",EDGE,{"derivedFrom":makeQuery(id+"F1.opExtrude","CAP_EDGE",EDGE,{"disambiguationData":[OSD([sQuery(id+"F0.wireOp",EDGE,"E73")])],"isStart":false})}),1.0]])]});
            var Q62;
            Q62=makeQuery(id+"F2.imprint","IMPRINT",FACE,{"disambiguationData":[TD([[makeQuery(id+"F2.imprint","IMPRINT",EDGE,{"derivedFrom":makeQuery(id+"F1.opExtrude","CAP_EDGE",EDGE,{"disambiguationData":[OSD([sQuery(id+"F0.wireOp",EDGE,"E74")])],"isStart":false})}),1.0]])]});
            var Q63;
            Q63=makeQuery(id+"F2.imprint","IMPRINT",FACE,{"disambiguationData":[TD([[makeQuery(id+"F2.imprint","IMPRINT",EDGE,{"derivedFrom":makeQuery(id+"F1.opExtrude","CAP_EDGE",EDGE,{"disambiguationData":[OSD([sQuery(id+"F0.wireOp",EDGE,"E75")])],"isStart":false})}),1.0]])]});
            var Q64;
            Q64=makeQuery(id+"F2.imprint","IMPRINT",FACE,{"disambiguationData":[TD([[makeQuery(id+"F2.imprint","IMPRINT",EDGE,{"derivedFrom":makeQuery(id+"F1.opExtrude","CAP_EDGE",EDGE,{"disambiguationData":[OSD([sQuery(id+"F0.wireOp",EDGE,"E76")])],"isStart":false})}),1.0]])]});
            var Q65;
            Q65=makeQuery(id+"F2.imprint","IMPRINT",FACE,{"disambiguationData":[TD([[makeQuery(id+"F2.imprint","IMPRINT",EDGE,{"derivedFrom":makeQuery(id+"F1.opExtrude","CAP_EDGE",EDGE,{"disambiguationData":[OSD([sQuery(id+"F0.wireOp",EDGE,"E77")])],"isStart":false})}),1.0]])]});
            var Q66;
            Q66=makeQuery(id+"F2.imprint","IMPRINT",FACE,{"disambiguationData":[TD([[makeQuery(id+"F2.imprint","IMPRINT",EDGE,{"derivedFrom":makeQuery(id+"F1.opExtrude","CAP_EDGE",EDGE,{"disambiguationData":[OSD([sQuery(id+"F0.wireOp",EDGE,"E78")])],"isStart":false})}),1.0]])]});
            var Q67;
            Q67=makeQuery(id+"F2.imprint","IMPRINT",FACE,{"disambiguationData":[TD([[makeQuery(id+"F2.imprint","IMPRINT",EDGE,{"derivedFrom":makeQuery(id+"F1.opExtrude","CAP_EDGE",EDGE,{"disambiguationData":[OSD([sQuery(id+"F0.wireOp",EDGE,"E79")])],"isStart":false})}),1.0]])]});
            var Q68;
            Q68=makeQuery(id+"F2.imprint","IMPRINT",FACE,{"disambiguationData":[TD([[makeQuery(id+"F2.imprint","IMPRINT",EDGE,{"derivedFrom":makeQuery(id+"F1.opExtrude","CAP_EDGE",EDGE,{"disambiguationData":[OSD([sQuery(id+"F0.wireOp",EDGE,"E80")])],"isStart":false})}),1.0]])]});
            var Q69;
            Q69=makeQuery(id+"F2.imprint","IMPRINT",FACE,{"disambiguationData":[TD([[makeQuery(id+"F2.imprint","IMPRINT",EDGE,{"derivedFrom":makeQuery(id+"F1.opExtrude","CAP_EDGE",EDGE,{"disambiguationData":[OSD([sQuery(id+"F0.wireOp",EDGE,"E81")])],"isStart":false})}),1.0]])]});
            var Q70;
            Q70=makeQuery(id+"F2.imprint","IMPRINT",FACE,{"disambiguationData":[TD([[makeQuery(id+"F2.imprint","IMPRINT",EDGE,{"derivedFrom":makeQuery(id+"F1.opExtrude","CAP_EDGE",EDGE,{"disambiguationData":[OSD([sQuery(id+"F0.wireOp",EDGE,"E82")])],"isStart":false})}),1.0]])]});
            var Q71;
            Q71=makeQuery(id+"F2.imprint","IMPRINT",FACE,{"disambiguationData":[TD([[makeQuery(id+"F2.imprint","IMPRINT",EDGE,{"derivedFrom":makeQuery(id+"F1.opExtrude","CAP_EDGE",EDGE,{"disambiguationData":[OSD([sQuery(id+"F0.wireOp",EDGE,"E83")])],"isStart":false})}),1.0]])]});
            var Q72;
            Q72=makeQuery(id+"F2.imprint","IMPRINT",FACE,{"disambiguationData":[TD([[makeQuery(id+"F2.imprint","IMPRINT",EDGE,{"derivedFrom":makeQuery(id+"F1.opExtrude","CAP_EDGE",EDGE,{"disambiguationData":[OSD([sQuery(id+"F0.wireOp",EDGE,"E84")])],"isStart":false})}),1.0]])]});
            var Q73;
            Q73=makeQuery(id+"F2.imprint","IMPRINT",FACE,{"disambiguationData":[TD([[makeQuery(id+"F2.imprint","IMPRINT",EDGE,{"derivedFrom":makeQuery(id+"F1.opExtrude","CAP_EDGE",EDGE,{"disambiguationData":[OSD([sQuery(id+"F0.wireOp",EDGE,"E85")])],"isStart":false})}),1.0]])]});
            var Q74;
            Q74=makeQuery(id+"F2.imprint","IMPRINT",FACE,{"disambiguationData":[TD([[makeQuery(id+"F2.imprint","IMPRINT",EDGE,{"derivedFrom":makeQuery(id+"F1.opExtrude","CAP_EDGE",EDGE,{"disambiguationData":[OSD([sQuery(id+"F0.wireOp",EDGE,"E86")])],"isStart":false})}),1.0]])]});
            var Q75;
            Q75=makeQuery(id+"F2.imprint","IMPRINT",FACE,{"disambiguationData":[TD([[makeQuery(id+"F2.imprint","IMPRINT",EDGE,{"derivedFrom":makeQuery(id+"F1.opExtrude","CAP_EDGE",EDGE,{"disambiguationData":[OSD([sQuery(id+"F0.wireOp",EDGE,"E87")])],"isStart":false})}),1.0]])]});
            var Q76;
            Q76=makeQuery(id+"F2.imprint","IMPRINT",FACE,{"disambiguationData":[TD([[makeQuery(id+"F2.imprint","IMPRINT",EDGE,{"derivedFrom":makeQuery(id+"F1.opExtrude","CAP_EDGE",EDGE,{"disambiguationData":[OSD([sQuery(id+"F0.wireOp",EDGE,"E88")])],"isStart":false})}),1.0]])]});
            var Q77;
            Q77=makeQuery(id+"F2.imprint","IMPRINT",FACE,{"disambiguationData":[TD([[makeQuery(id+"F2.imprint","IMPRINT",EDGE,{"derivedFrom":makeQuery(id+"F1.opExtrude","CAP_EDGE",EDGE,{"disambiguationData":[OSD([sQuery(id+"F0.wireOp",EDGE,"E89")])],"isStart":false})}),1.0]])]});
            var Q78;
            Q78=makeQuery(id+"F2.imprint","IMPRINT",FACE,{"disambiguationData":[TD([[makeQuery(id+"F2.imprint","IMPRINT",EDGE,{"derivedFrom":makeQuery(id+"F1.opExtrude","CAP_EDGE",EDGE,{"disambiguationData":[OSD([sQuery(id+"F0.wireOp",EDGE,"E90")])],"isStart":false})}),1.0]])]});
            var Q79;
            Q79=makeQuery(id+"F2.imprint","IMPRINT",FACE,{"disambiguationData":[TD([[makeQuery(id+"F2.imprint","IMPRINT",EDGE,{"derivedFrom":makeQuery(id+"F1.opExtrude","CAP_EDGE",EDGE,{"disambiguationData":[OSD([sQuery(id+"F0.wireOp",EDGE,"E91")])],"isStart":false})}),1.0]])]});
            var Q80;
            Q80=makeQuery(id+"F2.imprint","IMPRINT",FACE,{"disambiguationData":[TD([[makeQuery(id+"F2.imprint","IMPRINT",EDGE,{"derivedFrom":makeQuery(id+"F1.opExtrude","CAP_EDGE",EDGE,{"disambiguationData":[OSD([sQuery(id+"F0.wireOp",EDGE,"E92")])],"isStart":false})}),1.0]])]});
            var Q81;
            Q81=makeQuery(id+"F2.imprint","IMPRINT",FACE,{"disambiguationData":[TD([[makeQuery(id+"F2.imprint","IMPRINT",EDGE,{"derivedFrom":makeQuery(id+"F1.opExtrude","CAP_EDGE",EDGE,{"disambiguationData":[OSD([sQuery(id+"F0.wireOp",EDGE,"E93")])],"isStart":false})}),1.0]])]});
            var Q82;
            Q82=makeQuery(id+"F2.imprint","IMPRINT",FACE,{"disambiguationData":[TD([[makeQuery(id+"F2.imprint","IMPRINT",EDGE,{"derivedFrom":makeQuery(id+"F1.opExtrude","CAP_EDGE",EDGE,{"disambiguationData":[OSD([sQuery(id+"F0.wireOp",EDGE,"E94")])],"isStart":false})}),1.0]])]});
            var Q83;
            Q83=makeQuery(id+"F2.imprint","IMPRINT",FACE,{"disambiguationData":[TD([[makeQuery(id+"F2.imprint","IMPRINT",EDGE,{"derivedFrom":makeQuery(id+"F1.opExtrude","CAP_EDGE",EDGE,{"disambiguationData":[OSD([sQuery(id+"F0.wireOp",EDGE,"E96")])],"isStart":false})}),1.0]])]});
            var Q84;
            Q84=makeQuery(id+"F2.imprint","IMPRINT",FACE,{"disambiguationData":[TD([[makeQuery(id+"F2.imprint","IMPRINT",EDGE,{"derivedFrom":makeQuery(id+"F1.opExtrude","CAP_EDGE",EDGE,{"disambiguationData":[OSD([sQuery(id+"F0.wireOp",EDGE,"E97")])],"isStart":false})}),1.0]])]});
            var Q85;
            Q85=makeQuery(id+"F2.imprint","IMPRINT",FACE,{"disambiguationData":[TD([[makeQuery(id+"F2.imprint","IMPRINT",EDGE,{"derivedFrom":makeQuery(id+"F1.opExtrude","CAP_EDGE",EDGE,{"disambiguationData":[OSD([sQuery(id+"F0.wireOp",EDGE,"E98")])],"isStart":false})}),1.0]])]});
            var Q86;
            Q86=makeQuery(id+"F2.imprint","IMPRINT",FACE,{"disambiguationData":[TD([[makeQuery(id+"F2.imprint","IMPRINT",EDGE,{"derivedFrom":makeQuery(id+"F1.opExtrude","CAP_EDGE",EDGE,{"disambiguationData":[OSD([sQuery(id+"F0.wireOp",EDGE,"E99")])],"isStart":false})}),1.0]])]});
            var Q87;
            Q87=makeQuery(id+"F2.imprint","IMPRINT",FACE,{"disambiguationData":[TD([[makeQuery(id+"F2.imprint","IMPRINT",EDGE,{"derivedFrom":makeQuery(id+"F1.opExtrude","CAP_EDGE",EDGE,{"disambiguationData":[OSD([sQuery(id+"F0.wireOp",EDGE,"E100")])],"isStart":false})}),1.0]])]});
            var Q88;
            Q88=makeQuery(id+"F2.imprint","IMPRINT",FACE,{"disambiguationData":[TD([[makeQuery(id+"F2.imprint","IMPRINT",EDGE,{"derivedFrom":makeQuery(id+"F1.opExtrude","CAP_EDGE",EDGE,{"disambiguationData":[OSD([sQuery(id+"F0.wireOp",EDGE,"E101")])],"isStart":false})}),1.0]])]});
            var Q89;
            Q89=makeQuery(id+"F2.imprint","IMPRINT",FACE,{"disambiguationData":[TD([[makeQuery(id+"F2.imprint","IMPRINT",EDGE,{"derivedFrom":makeQuery(id+"F1.opExtrude","CAP_EDGE",EDGE,{"disambiguationData":[OSD([sQuery(id+"F0.wireOp",EDGE,"E102")])],"isStart":false})}),1.0]])]});
            var Q90;
            {var subQ15=sQuery(id+"F2.wireOp",EDGE,"E105");Q90=makeQuery(id+"F2.imprint","IMPRINT",FACE,{"disambiguationData":[TD([[makeQuery(id+"F2.imprint","IMPRINT",EDGE,{"derivedFrom":subQ15}),-1.0]])]});}
            extrude(context, id + "F3", {"entities" : qUnion([Q0, Q1, Q2, Q3, Q4, Q5, Q6, Q7, Q8, Q9, Q10, Q11, Q12, Q13, Q14, Q15, Q16, Q17, Q18, Q19, Q20, Q21, Q22, Q23, Q24, Q25, Q26, Q27, Q28, Q29, Q30, Q31, Q32, Q33, Q34, Q35, Q36, Q37, Q38, Q39, Q40, Q41, Q42, Q43, Q44, Q45, Q46, Q47, Q48, Q49, Q50, Q51, Q52, Q53, Q54, Q55, Q56, Q57, Q58, Q59, Q60, Q61, Q62, Q63, Q64, Q65, Q66, Q67, Q68, Q69, Q70, Q71, Q72, Q73, Q74, Q75, Q76, Q77, Q78, Q79, Q80, Q81, Q82, Q83, Q84, Q85, Q86, Q87, Q88, Q89, Q90]), "operationType" : NewBodyOperationType.REMOVE, "oppositeDirection" : true, "depth" : 8 * mm});
        }
    });
